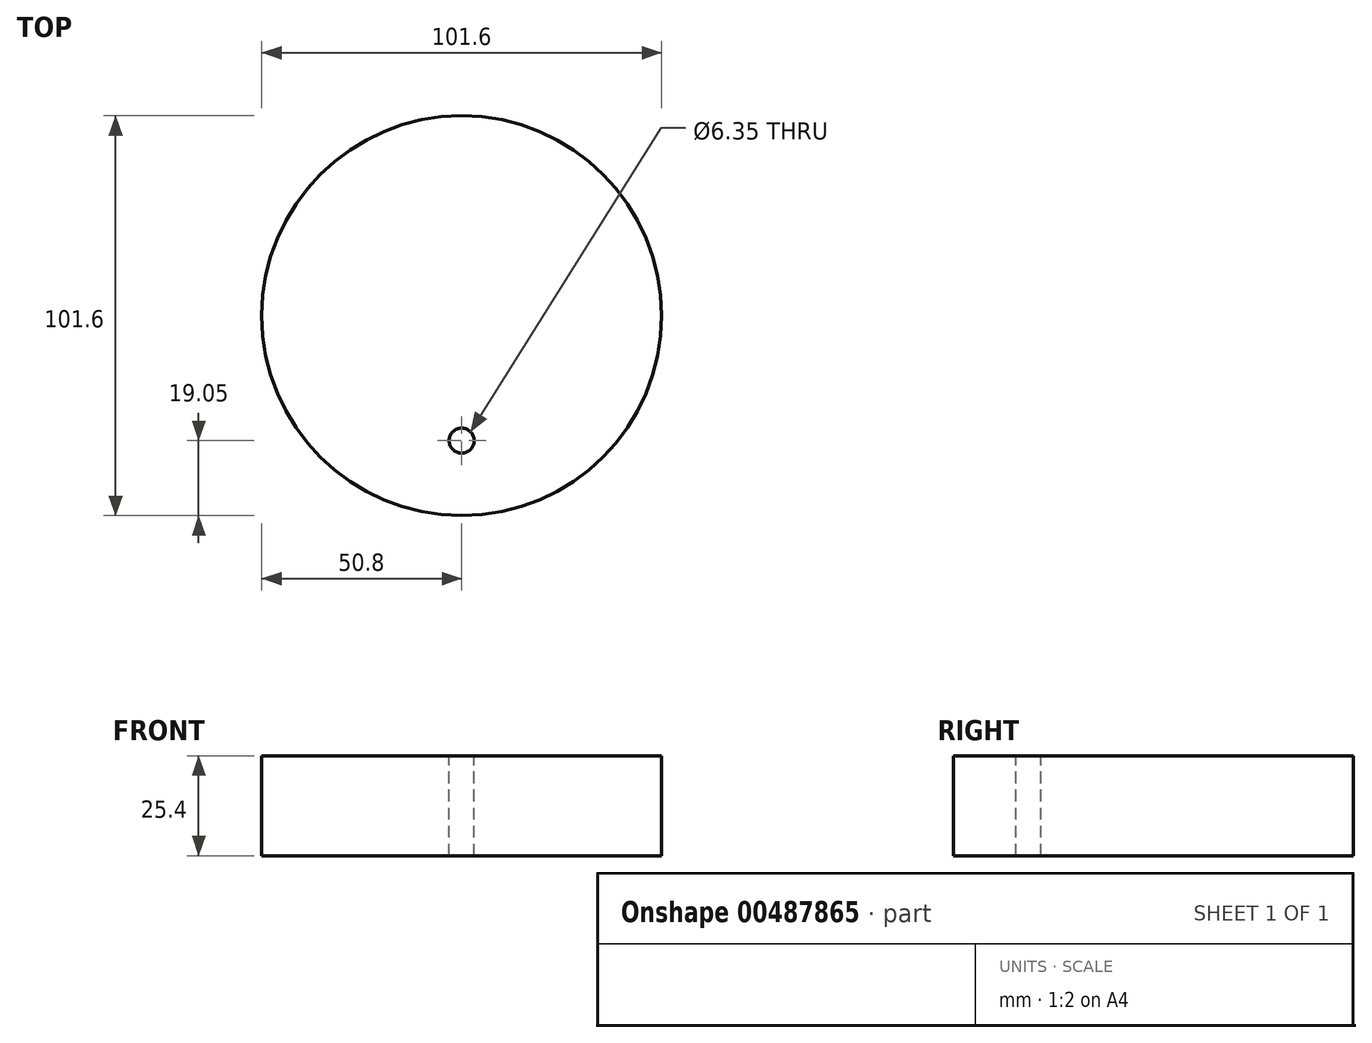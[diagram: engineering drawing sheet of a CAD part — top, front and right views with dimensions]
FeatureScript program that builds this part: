
annotation { "Feature Type Name" : "Feature", "Feature Type Description" : "" }
export const myFeature = defineFeature(function(context is Context, id is Id, definition is map)
    precondition{}
    {
        {
            var Q0;
            Q0=qCreatedBy(makeId("Top.planeOp"),FACE);
            var sketch = newSketch(context, id + "F0", { "sketchPlane" : qUnion([Q0])});
            skCircle(sketch, "E0", {"center": v(0, 0) * mm, "radius": 50.8 * mm});
            skSolve(sketch);
        }
        {
            var Q0;
            Q0=qSketchRegion(id+"F0",true);
            extrude(context, id + "F1", {"entities" : qUnion([Q0]), "depth" : 25.4 * mm});
        }
        {
            var Q0;
            Q0=makeQuery(id+"F1.opExtrude","CAP_FACE",FACE,{"disambiguationData":[OSD([sQuery(id+"F0.wireOp",EDGE,"E0")])],"isStart":false});
            var sketch = newSketch(context, id + "F2", { "sketchPlane" : qUnion([Q0])});
            skCircle(sketch, "E1", {"center": v(0, 0) * mm, "radius": 31.75 * mm, "construction": true});
            skCircle(sketch, "E2", {"center": v(0, -31.75) * mm, "radius": 3.18 * mm});
            skSolve(sketch);
        }
        {
            var Q0;
            Q0=makeQuery(id+"F2.imprint","IMPRINT",FACE,{"disambiguationData":[TD([[makeQuery(id+"F2.imprint","IMPRINT",EDGE,{"derivedFrom":sQuery(id+"F2.wireOp",EDGE,"E2")}),1.0]])]});
            extrude(context, id + "F3", {"entities" : qUnion([Q0]), "operationType" : NewBodyOperationType.REMOVE, "endBound" : BoundingType.THROUGH_ALL, "oppositeDirection" : true, "depth" : 25.4 * mm});
        }
    });
